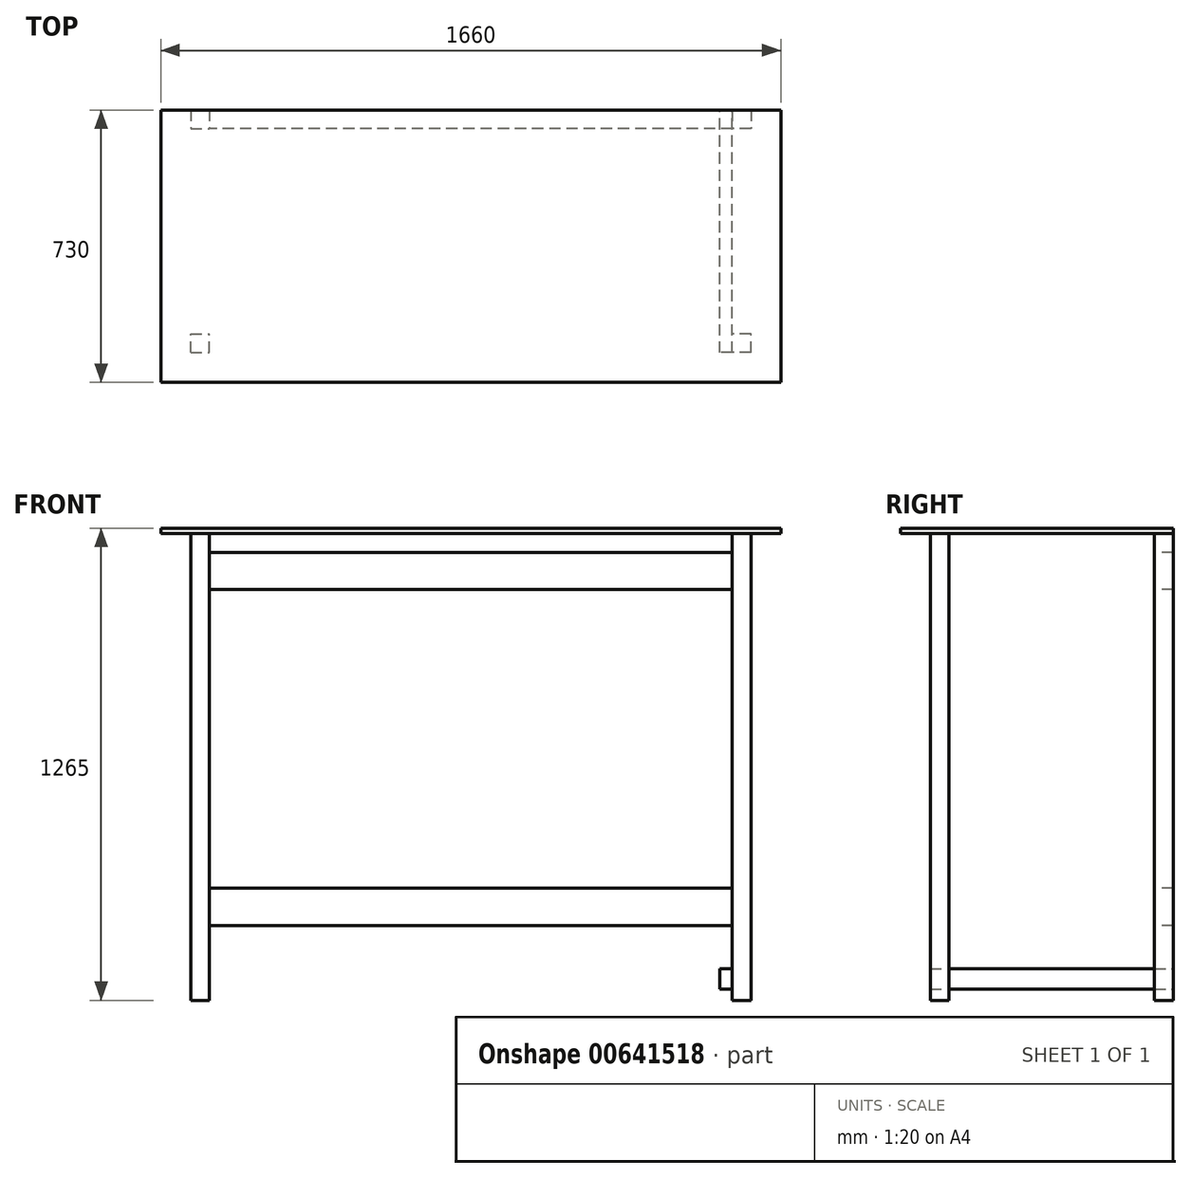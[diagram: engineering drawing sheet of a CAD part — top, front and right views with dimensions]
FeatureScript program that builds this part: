
annotation { "Feature Type Name" : "Feature", "Feature Type Description" : "" }
export const myFeature = defineFeature(function(context is Context, id is Id, definition is map)
    precondition{}
    {
        {
            var Q0;
            Q0=qCreatedBy(makeId("Top.planeOp"),FACE);
            var sketch = newSketch(context, id + "F0", { "sketchPlane" : qUnion([Q0])});
            skLineSegment(sketch, "E0.bottom", {"start": v(0, 0) * mm, "end": v(1500, 0) * mm, "construction": true});
            skLineSegment(sketch, "E0.top", {"start": v(0, 650) * mm, "end": v(1500, 650) * mm, "construction": true});
            skLineSegment(sketch, "E0.left", {"start": v(0, 0) * mm, "end": v(0, 650) * mm, "construction": true});
            skLineSegment(sketch, "E0.right", {"start": v(1500, 0) * mm, "end": v(1500, 650) * mm, "construction": true});
            skLineSegment(sketch, "E1.bottom", {"start": v(0, 0) * mm, "end": v(50, 0) * mm});
            skLineSegment(sketch, "E1.top", {"start": v(0, 50) * mm, "end": v(50, 50) * mm});
            skLineSegment(sketch, "E1.left", {"start": v(0, 0) * mm, "end": v(0, 50) * mm});
            skLineSegment(sketch, "E1.right", {"start": v(50, 0) * mm, "end": v(50, 50) * mm});
            skLineSegment(sketch, "E2.bottom", {"start": v(1500, 0) * mm, "end": v(1450, 0) * mm});
            skLineSegment(sketch, "E2.top", {"start": v(1500, 50) * mm, "end": v(1450, 50) * mm});
            skLineSegment(sketch, "E2.left", {"start": v(1500, 0) * mm, "end": v(1500, 50) * mm});
            skLineSegment(sketch, "E2.right", {"start": v(1450, 0) * mm, "end": v(1450, 50) * mm});
            skLineSegment(sketch, "E3.bottom", {"start": v(1500, 650) * mm, "end": v(1450, 650) * mm});
            skLineSegment(sketch, "E3.top", {"start": v(1500, 600) * mm, "end": v(1450, 600) * mm});
            skLineSegment(sketch, "E3.left", {"start": v(1500, 650) * mm, "end": v(1500, 600) * mm});
            skLineSegment(sketch, "E3.right", {"start": v(1450, 650) * mm, "end": v(1450, 600) * mm});
            skLineSegment(sketch, "E4.bottom", {"start": v(0, 650) * mm, "end": v(50, 650) * mm});
            skLineSegment(sketch, "E4.top", {"start": v(0, 600) * mm, "end": v(50, 600) * mm});
            skLineSegment(sketch, "E4.left", {"start": v(0, 650) * mm, "end": v(0, 600) * mm});
            skLineSegment(sketch, "E4.right", {"start": v(50, 650) * mm, "end": v(50, 600) * mm});
            skSolve(sketch);
        }
        {
            var Q0;
            Q0 = qSketchRegion(id + "F0", true);
            extrude(context, id + "F1", {"entities" : qUnion([Q0]), "depth" : 1250 * mm, "offsetDistance" : 25 * mm});
        }
        {
            var Q0;
            Q0=makeQuery(id+"F1.opExtrude","CAP_FACE",FACE,{"disambiguationData":[OSD([sQuery(id+"F0.wireOp",EDGE,"E1.bottom"),sQuery(id+"F0.wireOp",EDGE,"E1.top"),sQuery(id+"F0.wireOp",EDGE,"E1.left"),sQuery(id+"F0.wireOp",EDGE,"E1.right")])],"isStart":false});
            var sketch = newSketch(context, id + "F2", { "sketchPlane" : qUnion([Q0])});
            skLineSegment(sketch, "E5.bottom", {"start": v(-80, -80) * mm, "end": v(1580, -80) * mm});
            skLineSegment(sketch, "E5.top", {"start": v(-80, 650) * mm, "end": v(1580, 650) * mm});
            skLineSegment(sketch, "E5.left", {"start": v(-80, -80) * mm, "end": v(-80, 650) * mm});
            skLineSegment(sketch, "E5.right", {"start": v(1580, -80) * mm, "end": v(1580, 650) * mm});
            skSolve(sketch);
        }
        {
            var Q0;
            Q0=makeQuery(id+"F2.imprint","IMPRINT",FACE,{"disambiguationData":[TD([[makeQuery(id+"F2.imprint","IMPRINT",EDGE,{"derivedFrom":sQuery(id+"F2.wireOp",EDGE,"E5.bottom")}),1.0]])]});
            var Q1;
            Q1=makeQuery(id+"F2.imprint","IMPRINT",FACE,{"disambiguationData":[TD([[makeQuery(id+"F2.imprint","IMPRINT",EDGE,{"derivedFrom":makeQuery(id+"F1.opExtrude","CAP_EDGE",EDGE,{"disambiguationData":[OSD([sQuery(id+"F0.wireOp",EDGE,"E1.bottom")])],"isStart":false})}),1.0]])]});
            extrude(context, id + "F3", {"entities" : qUnion([Q0, Q1]), "depth" : 15 * mm, "offsetDistance" : 25 * mm});
        }
        {
            var Q0;
            Q0=makeQuery(id+"F1.opExtrude","SWEPT_FACE",FACE,{"disambiguationData":[OSD([sQuery(id+"F0.wireOp",EDGE,"E4.right")])]});
            var sketch = newSketch(context, id + "F4", { "sketchPlane" : qUnion([Q0])});
            skLineSegment(sketch, "E6.bottom", {"start": v(650, 200) * mm, "end": v(600, 200) * mm});
            skLineSegment(sketch, "E6.top", {"start": v(650, 300) * mm, "end": v(600, 300) * mm});
            skLineSegment(sketch, "E6.left", {"start": v(650, 200) * mm, "end": v(650, 300) * mm});
            skLineSegment(sketch, "E6.right", {"start": v(600, 200) * mm, "end": v(600, 300) * mm});
            skLineSegment(sketch, "E7.bottom", {"start": v(650, 1100) * mm, "end": v(600, 1100) * mm});
            skLineSegment(sketch, "E7.top", {"start": v(650, 1200) * mm, "end": v(600, 1200) * mm});
            skLineSegment(sketch, "E7.left", {"start": v(650, 1100) * mm, "end": v(650, 1200) * mm});
            skLineSegment(sketch, "E7.right", {"start": v(600, 1100) * mm, "end": v(600, 1200) * mm});
            skSolve(sketch);
        }
        {
            var Q0;
            Q0 = qSketchRegion(id + "F4", true);
            extrude(context, id + "F5", {"entities" : qUnion([Q0]), "endBound" : BoundingType.UP_TO_NEXT, "depth" : 25 * mm, "offsetDistance" : 25 * mm});
        }
        {
            var Q0;
            Q0=makeQuery(id+"F1.opExtrude","SWEPT_FACE",FACE,{"disambiguationData":[OSD([sQuery(id+"F0.wireOp",EDGE,"E3.top")])]});
            var sketch = newSketch(context, id + "F6", { "sketchPlane" : qUnion([Q0])});
            skLineSegment(sketch, "E8.bottom", {"start": v(1450, 30) * mm, "end": v(1416, 30) * mm});
            skLineSegment(sketch, "E8.top", {"start": v(1450, 84) * mm, "end": v(1416, 84) * mm});
            skLineSegment(sketch, "E8.left", {"start": v(1450, 30) * mm, "end": v(1450, 84) * mm});
            skLineSegment(sketch, "E8.right", {"start": v(1416, 30) * mm, "end": v(1416, 84) * mm});
            skSolve(sketch);
        }
        {
            var Q0;
            Q0 = qSketchRegion(id + "F6", true);
            extrude(context, id + "F7", {"entities" : qUnion([Q0]), "depth" : 600 * mm, "offsetDistance" : 25 * mm, "hasSecondDirection" : true, "secondDirectionOppositeDirection" : true, "secondDirectionDepth" : 50 * mm});
        }
    });
